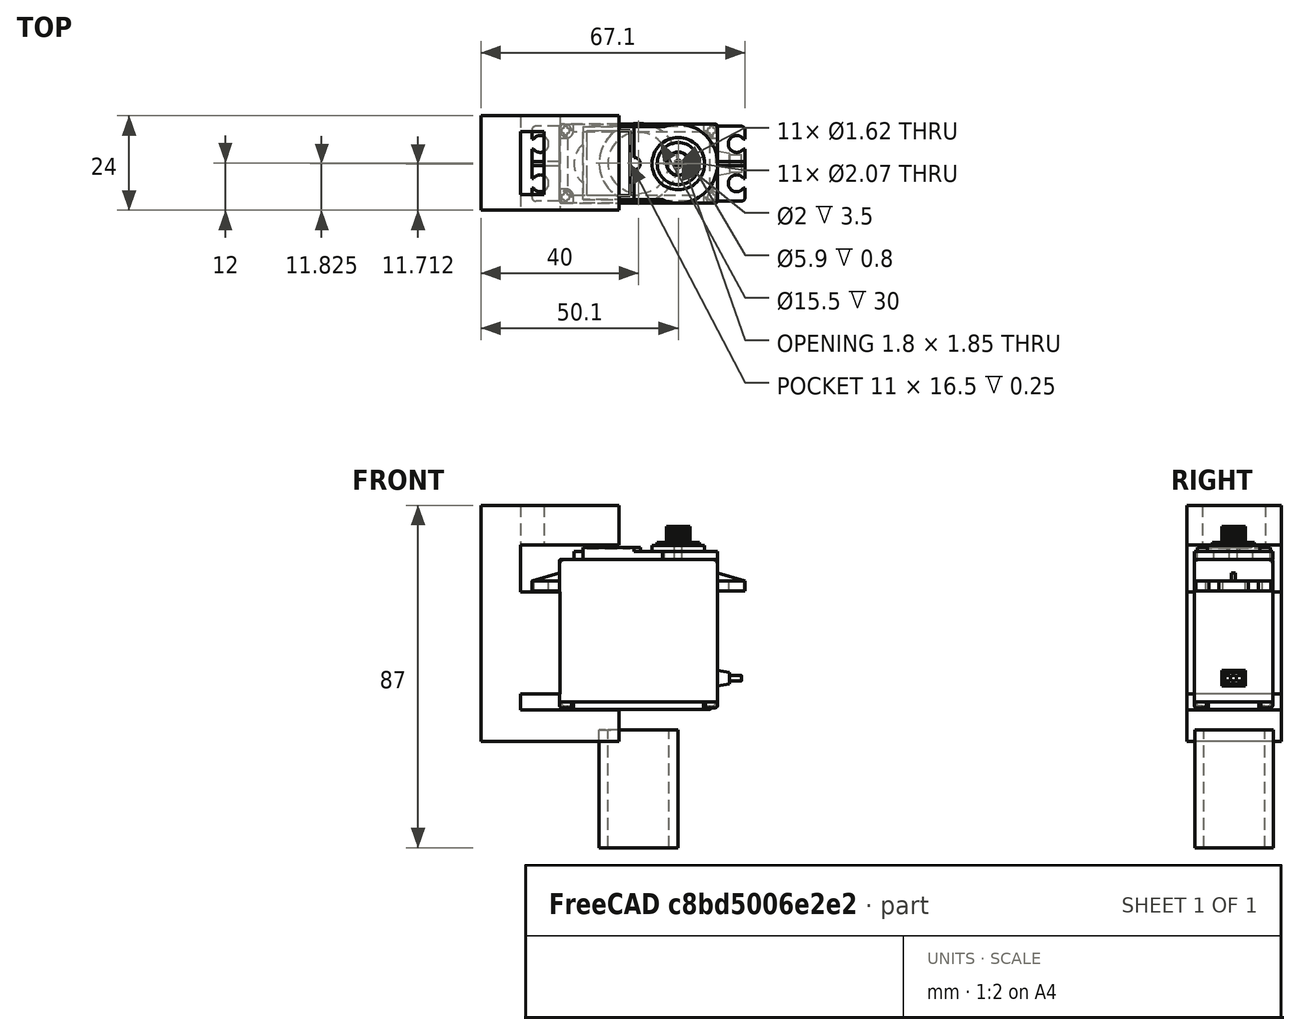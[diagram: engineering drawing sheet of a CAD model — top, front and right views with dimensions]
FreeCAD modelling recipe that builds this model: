
FCSTD DOCUMENT  (FreeCAD 0.21R33771 (Git))
Label: U_Servo_angulo_v1
License: All rights reserved
LicenseURL: http://en.wikipedia.org/wiki/All_rights_reserved
objects: Mesh::Feature×2, Sketcher::SketchObject×2, Part::FeaturePython×1, Part::Feature×1, PartDesign::Pad×1, PartDesign::Pocket×1, PartDesign::Body×1
note: 9 computed .brp shape members not serialized (recipe doc carries the construction recipe); baked Part::Feature solids carry a one-line shape summary decoded from their .brp

FEATURE [Part::FeaturePython] Tube  # WARN: FeaturePython — macro-defined, semantics opaque (R4)
  AttacherType = Attacher::AttachEngine3D
  Height = 30
  InnerRadius = 7.75
  OuterRadius = 10
  Placement = pos=(0,-12,-37) rot=(0,0,1;0rad)
FEATURE [Mesh::Feature] servo_lower_cover_fake_shaft
  Placement = pos=(0,-12,2) rot=(0,1,0;3.14159rad)
FEATURE [Part::Feature] Part__Feature  label="MG996R"
  Placement = pos=(0,-9,-0.5) rot=(0,0,1;0rad)
  shape: bbox 54.21 x 20.13 x 46.64 mm, 453 faces, 11 solids (baked)
FEATURE [Mesh::Feature] futaba  label="Servo"
  Placement = pos=(0,-3,2) rot=(0,0,1;0rad)
FEATURE [Sketcher::SketchObject] Sketch
  FullyConstrained = false
  MapMode = 5
  Placement = pos=(0,0,0) rot=(1,0,0;1.5708rad)
  Support = -> [XZ_Plane]
  sketch-geometry (12):
    g0: LineSegment StartX=-5 StartY=39.9337 StartZ=0 EndX=-30 EndY=39.9337 EndZ=0
    g1: LineSegment StartX=-5 StartY=50 StartZ=0 EndX=-40 EndY=50 EndZ=0
    g2: LineSegment StartX=-20 StartY=28 StartZ=0 EndX=-30 EndY=28 EndZ=0
    g3: LineSegment StartX=-20 StartY=2.0296 StartZ=0 EndX=-30 EndY=2.0296 EndZ=0
    g4: LineSegment StartX=-40 StartY=-10 StartZ=0 EndX=-5 EndY=-10 EndZ=0
    g5: LineSegment StartX=-5 StartY=-2 StartZ=0 EndX=-30 EndY=-2 EndZ=0
    g6: LineSegment StartX=-40 StartY=50 StartZ=0 EndX=-40 EndY=-10 EndZ=0
    g7: LineSegment StartX=-5 StartY=-10 StartZ=0 EndX=-5 EndY=-2 EndZ=0
    g8: LineSegment StartX=-30 StartY=-2 StartZ=0 EndX=-30 EndY=2.0296 EndZ=0
    g9: LineSegment StartX=-20 StartY=28 StartZ=0 EndX=-20 EndY=2.0296 EndZ=0
    g10: LineSegment StartX=-30 StartY=28 StartZ=0 EndX=-30 EndY=39.9337 EndZ=0
    g11: LineSegment StartX=-5 StartY=39.9337 StartZ=0 EndX=-5 EndY=50 EndZ=0
  constraints (24):
    c: Horizontal(g0)
    c: Horizontal(g1)
    c: Horizontal(g2)
    c: Horizontal(g3)
    c: Horizontal(g4)
    c: Horizontal(g5)
    c: Coincident(g6,g1)
    c: Coincident(g6,g4)
    c: Vertical(g6)
    c: Coincident(g7,g4)
    c: Coincident(g7,g5)
    c: Vertical(g7)
    c: Coincident(g8,g5)
    c: Coincident(g8,g3)
    c: Vertical(g8)
    c: Coincident(g9,g2)
    c: Coincident(g9,g3)
    c: Vertical(g9)
    c: Coincident(g10,g2)
    c: Coincident(g10,g0)
    c: Vertical(g10)
    c: Coincident(g11,g0)
    c: Coincident(g11,g1)
    c: Vertical(g11)
FEATURE [PartDesign::Pad] Pad
  Direction = (0,-1,-2e-16)
  Length = 24
  Length2 = 10
  Placement = pos=(0,0,0) rot=(1,0,0;1.5708rad)
  Profile = -> Sketch
  ReferenceAxis = -> Sketch [N_Axis]
  Type = 0
FEATURE [Sketcher::SketchObject] Sketch001
  FullyConstrained = false
  MapMode = 5
  Placement = pos=(0,-1.11e-14,50) rot=(0,0,1;3.14159rad)
  Support = -> [Pad]
  sketch-geometry (4):
    g0: LineSegment StartX=24 StartY=20.048 StartZ=0 EndX=30 EndY=20.048 EndZ=0
    g1: LineSegment StartX=30 StartY=20.048 StartZ=0 EndX=30 EndY=4.04802 EndZ=0
    g2: LineSegment StartX=30 StartY=4.04802 StartZ=0 EndX=24 EndY=4.04802 EndZ=0
    g3: LineSegment StartX=24 StartY=4.04802 StartZ=0 EndX=24 EndY=20.048 EndZ=0
  constraints (8):
    c: Coincident(g0,g1)
    c: Coincident(g1,g2)
    c: Coincident(g2,g3)
    c: Coincident(g3,g0)
    c: Horizontal(g0)
    c: Horizontal(g2)
    c: Vertical(g1)
    c: Vertical(g3)
FEATURE [PartDesign::Pocket] Pocket
  BaseFeature = -> Pad
  Direction = (0,2e-16,-1)
  Length = 11
  Length2 = 5
  Placement = pos=(0,0,0) rot=(1,0,0;1.5708rad)
  Profile = -> Sketch001
  ReferenceAxis = -> Sketch001 [N_Axis]
  Type = 0
FEATURE [PartDesign::Body] Body
  Group = -> [Sketch,Pad,Sketch001,Pocket]
  Origin = -> Origin
  Tip = -> Pocket
